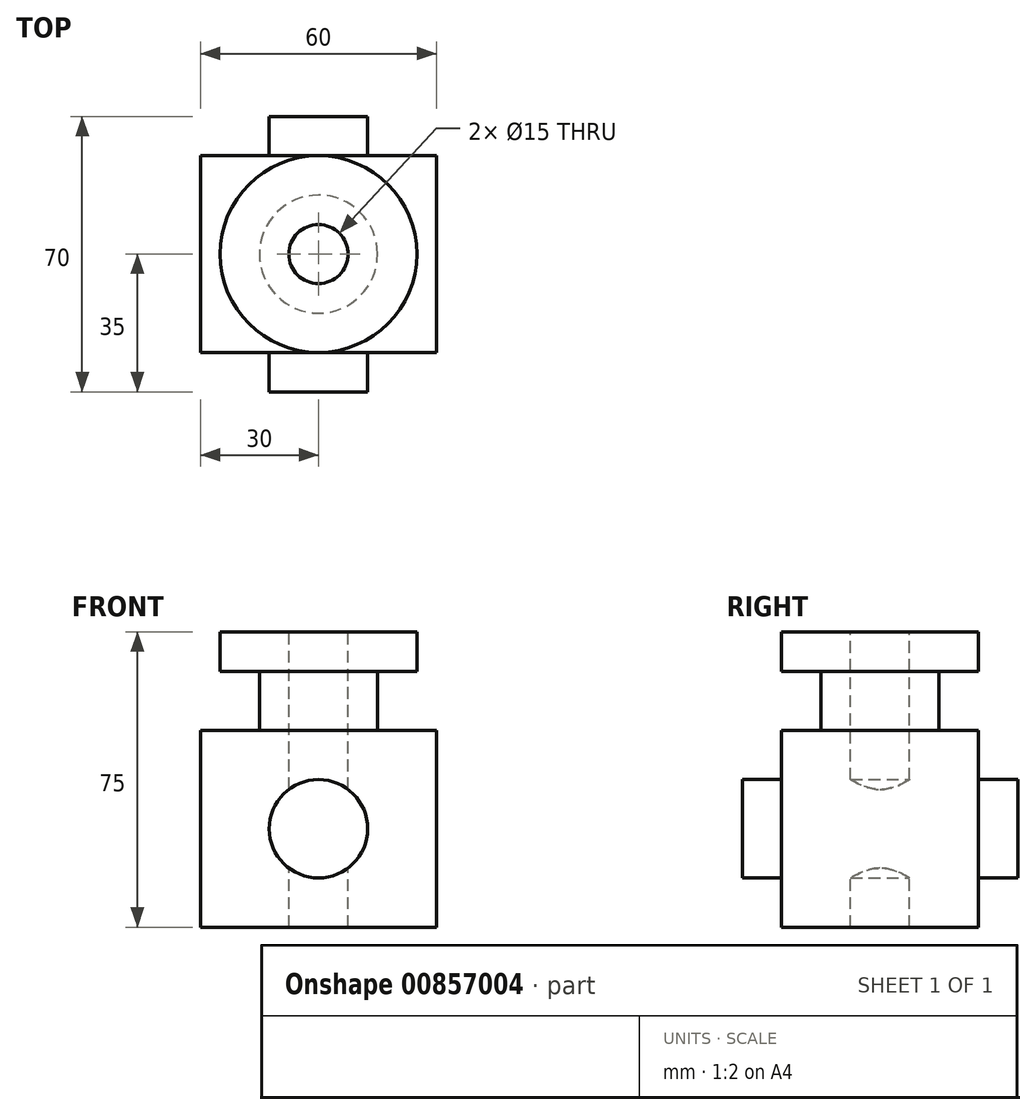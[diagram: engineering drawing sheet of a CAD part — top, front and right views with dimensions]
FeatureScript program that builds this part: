
annotation { "Feature Type Name" : "Feature", "Feature Type Description" : "" }
export const myFeature = defineFeature(function(context is Context, id is Id, definition is map)
    precondition{}
    {
        {
            var Q0;
            Q0=qCreatedBy(makeId("Top.planeOp"),FACE);
            var sketch = newSketch(context, id + "F0", { "sketchPlane" : qUnion([Q0])});
            skLineSegment(sketch, "E0.bottom", {"start": v(30, 25) * mm, "end": v(-30, 25) * mm});
            skLineSegment(sketch, "E0.top", {"start": v(30, -25) * mm, "end": v(-30, -25) * mm});
            skLineSegment(sketch, "E0.left", {"start": v(30, 25) * mm, "end": v(30, -25) * mm});
            skLineSegment(sketch, "E0.right", {"start": v(-30, 25) * mm, "end": v(-30, -25) * mm});
            skPoint(sketch, "E0.middle", {"position": v(0, 0) * mm});
            skSolve(sketch);
        }
        {
            var Q0;
            Q0 = qSketchRegion(id + "F0", true);
            extrude(context, id + "F1", {"entities" : qUnion([Q0]), "depth" : 25 * mm, "offsetDistance" : 25 * mm, "hasSecondDirection" : true, "secondDirectionOppositeDirection" : true, "secondDirectionDepth" : 25 * mm});
        }
        {
            var Q0;
            Q0=qCreatedBy(makeId("Front.planeOp"),FACE);
            var sketch = newSketch(context, id + "F2", { "sketchPlane" : qUnion([Q0])});
            skLineSegment(sketch, "E1", {"start": v(-15, 25) * mm, "end": v(-15, 40) * mm});
            skLineSegment(sketch, "E2", {"start": v(-15, 40) * mm, "end": v(-25, 40) * mm});
            skLineSegment(sketch, "E3", {"start": v(-25, 40) * mm, "end": v(-25, 50) * mm});
            skLineSegment(sketch, "E4", {"start": v(-25, 50) * mm, "end": v(0, 50) * mm});
            skLineSegment(sketch, "E5", {"start": v(0, 50) * mm, "end": v(0, 25) * mm});
            skLineSegment(sketch, "E6", {"start": v(-15, 25) * mm, "end": v(0, 25) * mm});
            skSolve(sketch);
        }
        {
            var Q0;
            Q0 = qSketchRegion(id + "F2", true);
            var Q1;
            Q1=sQuery(id+"F2.wireOp",EDGE,"E5");
            revolve(context, id + "F3", {"operationType" : NewBodyOperationType.ADD, "surfaceOperationType" : NewSurfaceOperationType.NEW, "entities" : qUnion([Q0]), "axis" : qUnion([Q1]), "revolveType" : RevolveType.FULL});
        }
        {
            var Q0;
            Q0=makeQuery(id+"F3.opRevolve","SWEPT_FACE",FACE,{"disambiguationData":[OSD([sQuery(id+"F2.wireOp",EDGE,"E4")])]});
            var sketch = newSketch(context, id + "F4", { "sketchPlane" : qUnion([Q0])});
            skCircle(sketch, "E7", {"center": v(0, 0) * mm, "radius": 7.5 * mm});
            skSolve(sketch);
        }
        {
            var Q0;
            Q0 = qSketchRegion(id + "F4", true);
            extrude(context, id + "F5", {"entities" : qUnion([Q0]), "operationType" : NewBodyOperationType.REMOVE, "endBound" : BoundingType.THROUGH_ALL, "oppositeDirection" : true, "depth" : 25 * mm, "offsetDistance" : 25 * mm});
        }
        {
            var Q0;
            Q0=qCreatedBy(makeId("Front.planeOp"),FACE);
            var sketch = newSketch(context, id + "F6", { "sketchPlane" : qUnion([Q0])});
            skCircle(sketch, "E8", {"center": v(0, 0) * mm, "radius": 12.5 * mm});
            skSolve(sketch);
        }
        {
            var Q0;
            Q0 = qSketchRegion(id + "F6", true);
            extrude(context, id + "F7", {"entities" : qUnion([Q0]), "operationType" : NewBodyOperationType.ADD, "depth" : 35 * mm, "offsetDistance" : 25 * mm, "hasSecondDirection" : true, "secondDirectionOppositeDirection" : true, "secondDirectionDepth" : 35 * mm});
        }
    });
